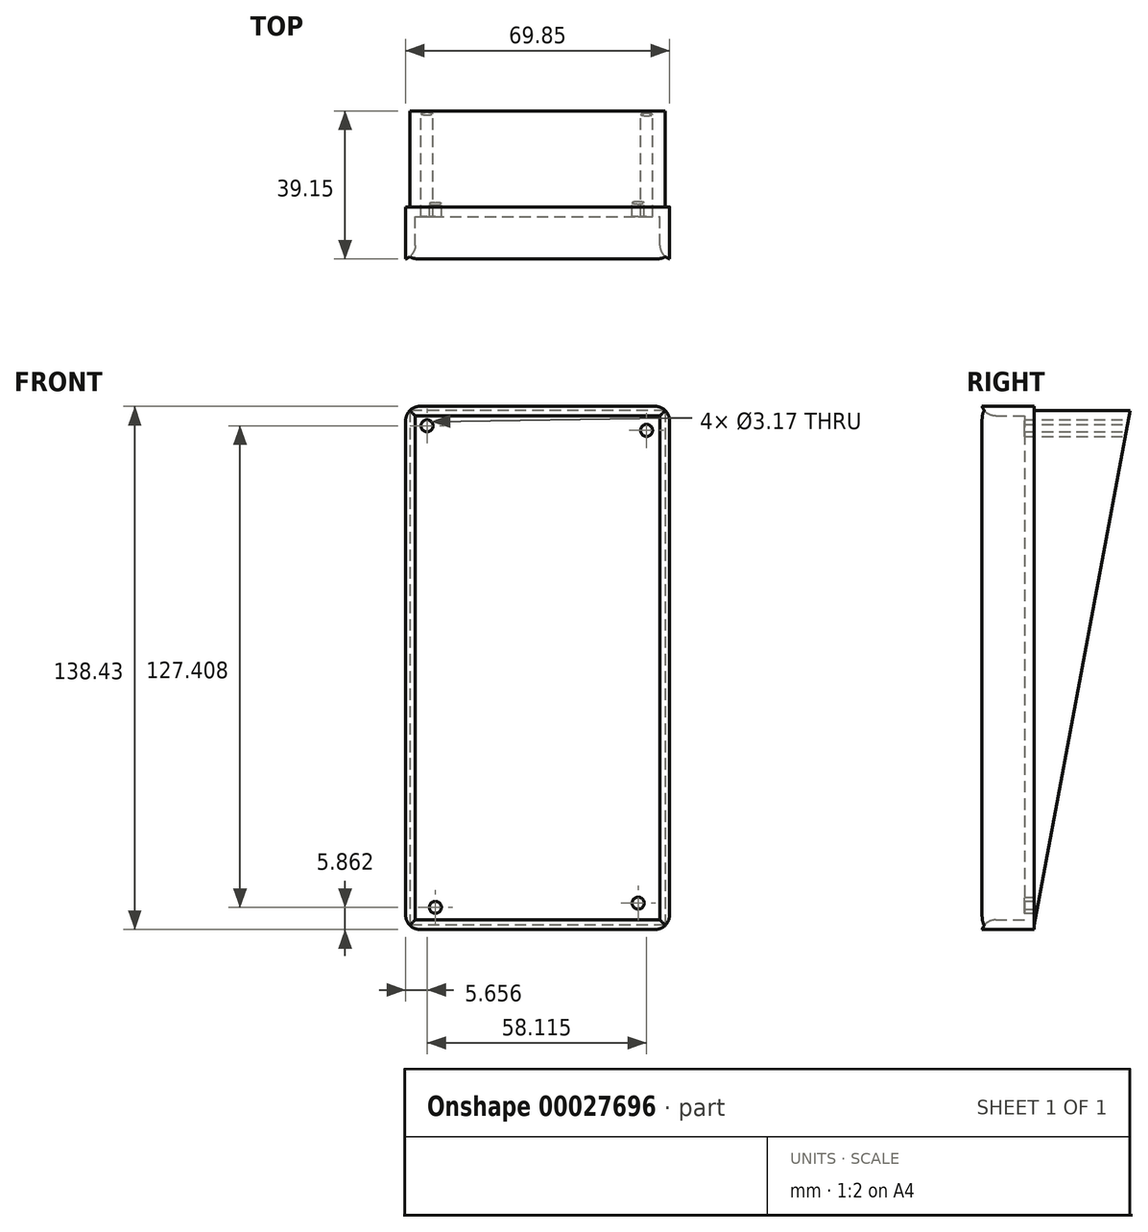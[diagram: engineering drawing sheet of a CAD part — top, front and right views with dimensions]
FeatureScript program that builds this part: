
annotation { "Feature Type Name" : "Feature", "Feature Type Description" : "" }
export const myFeature = defineFeature(function(context is Context, id is Id, definition is map)
    precondition{}
    {
        {
            var Q0;
            Q0=qCreatedBy(makeId("Front.planeOp"),FACE);
            var sketch = newSketch(context, id + "F0", { "sketchPlane" : qUnion([Q0])});
            skLineSegment(sketch, "E0.bottom", {"start": v(-34.53, 80.9) * mm, "end": v(35.32, 80.9) * mm});
            skLineSegment(sketch, "E0.top", {"start": v(-34.53, -57.52) * mm, "end": v(35.32, -57.52) * mm});
            skLineSegment(sketch, "E0.left", {"start": v(-34.53, 80.9) * mm, "end": v(-34.53, -57.52) * mm});
            skLineSegment(sketch, "E0.right", {"start": v(35.32, 80.9) * mm, "end": v(35.32, -57.52) * mm});
            skSolve(sketch);
        }
        {
            var Q0;
            Q0 = qSketchRegion(id + "F0", true);
            extrude(context, id + "F1", {"entities" : qUnion([Q0]), "depth" : 13.97 * mm});
        }
        {
            var Q0;
            Q0=makeQuery(id+"F1.opExtrude","CAP_FACE",FACE,{"disambiguationData":[OSD([sQuery(id+"F0.wireOp",EDGE,"E0.bottom"),sQuery(id+"F0.wireOp",EDGE,"E0.top"),sQuery(id+"F0.wireOp",EDGE,"E0.left"),sQuery(id+"F0.wireOp",EDGE,"E0.right")])],"isStart":false});
            shell(context, id + "F2", {"entities" : qUnion([Q0]), "thickness" : 2.54 * mm});
        }
        {
            var Q0;
            {var subQ0=sQuery(id+"F0.wireOp",EDGE,"E0.bottom");Q0=makeQuery(id+"F2.opShell","OFFSET_EDGE",EDGE,{"disambiguationData":[OSD([subQ0]),TDD([makeQuery(id+"F1.opExtrude","CAP_EDGE",EDGE,{"disambiguationData":[OSD([subQ0])],"isStart":false})])]});}
            var Q1;
            {var subQ0=sQuery(id+"F0.wireOp",EDGE,"E0.left");Q1=makeQuery(id+"F2.opShell","OFFSET_EDGE",EDGE,{"disambiguationData":[OSD([subQ0]),TDD([makeQuery(id+"F1.opExtrude","CAP_EDGE",EDGE,{"disambiguationData":[OSD([subQ0])],"isStart":false})])]});}
            var Q2;
            {var subQ0=sQuery(id+"F0.wireOp",EDGE,"E0.right");Q2=makeQuery(id+"F2.opShell","OFFSET_EDGE",EDGE,{"disambiguationData":[OSD([subQ0]),TDD([makeQuery(id+"F1.opExtrude","CAP_EDGE",EDGE,{"disambiguationData":[OSD([subQ0])],"isStart":false})])]});}
            var Q3;
            {var subQ0=sQuery(id+"F0.wireOp",EDGE,"E0.top");Q3=makeQuery(id+"F2.opShell","OFFSET_EDGE",EDGE,{"disambiguationData":[OSD([subQ0]),TDD([makeQuery(id+"F1.opExtrude","CAP_EDGE",EDGE,{"disambiguationData":[OSD([subQ0])],"isStart":false})])]});}
            var Q4;
            Q4=makeQuery(id+"F1.opExtrude","SWEPT_EDGE",EDGE,{"disambiguationData":[OSD([sQuery(id+"F0.wireOp",EDGE,"E0.top"),sQuery(id+"F0.wireOp",EDGE,"E0.left")])]});
            var Q5;
            Q5=makeQuery(id+"F1.opExtrude","SWEPT_EDGE",EDGE,{"disambiguationData":[OSD([sQuery(id+"F0.wireOp",EDGE,"E0.top"),sQuery(id+"F0.wireOp",EDGE,"E0.right")])]});
            var Q6;
            Q6=makeQuery(id+"F1.opExtrude","SWEPT_EDGE",EDGE,{"disambiguationData":[OSD([sQuery(id+"F0.wireOp",EDGE,"E0.bottom"),sQuery(id+"F0.wireOp",EDGE,"E0.left")])]});
            var Q7;
            Q7=makeQuery(id+"F1.opExtrude","SWEPT_EDGE",EDGE,{"disambiguationData":[OSD([sQuery(id+"F0.wireOp",EDGE,"E0.bottom"),sQuery(id+"F0.wireOp",EDGE,"E0.right")])]});
            fillet(context, id + "F3", {"entities" : qUnion([Q0, Q1, Q2, Q3, Q4, Q5, Q6, Q7]), "radius" : 3.8 * mm, "tangentPropagation" : true, "allowEdgeOverflow" : false});
        }
        {
            var Q0;
            Q0=makeQuery(id+"F1.opExtrude","CAP_FACE",FACE,{"disambiguationData":[OSD([sQuery(id+"F0.wireOp",EDGE,"E0.bottom"),sQuery(id+"F0.wireOp",EDGE,"E0.top"),sQuery(id+"F0.wireOp",EDGE,"E0.left"),sQuery(id+"F0.wireOp",EDGE,"E0.right")])],"isStart":true});
            var sketch = newSketch(context, id + "F4", { "sketchPlane" : qUnion([Q0])});
            skLineSegment(sketch, "E1.bottom", {"start": v(-34.2, 79.8) * mm, "end": v(33.42, 79.8) * mm});
            skLineSegment(sketch, "E1.top", {"start": v(-34.2, -56.4) * mm, "end": v(33.42, -56.4) * mm});
            skLineSegment(sketch, "E1.left", {"start": v(-34.2, 79.8) * mm, "end": v(-34.2, -56.4) * mm});
            skLineSegment(sketch, "E1.right", {"start": v(33.42, 79.8) * mm, "end": v(33.42, -56.4) * mm});
            skSolve(sketch);
        }
        {
            var Q0;
            Q0=makeQuery(id+"F4.imprint","IMPRINT",FACE,{"disambiguationData":[TD([[makeQuery(id+"F4.imprint","IMPRINT",EDGE,{"derivedFrom":sQuery(id+"F4.wireOp",EDGE,"E1.bottom")}),-1.0]])]});
            extrude(context, id + "F5", {"entities" : qUnion([Q0]), "operationType" : NewBodyOperationType.ADD, "depth" : 50.8 * mm});
        }
        {
            var Q0;
            Q0=makeQuery(id+"F5.opExtrude","SWEPT_FACE",FACE,{"disambiguationData":[OSD([sQuery(id+"F4.wireOp",EDGE,"E1.left")])]});
            var sketch = newSketch(context, id + "F6", { "sketchPlane" : qUnion([Q0])});
            skLineSegment(sketch, "E2", {"start": v(25.4, 79.8) * mm, "end": v(0, -56.4) * mm});
            skSolve(sketch);
        }
        {
            var Q0;
            Q0=makeQuery(id+"F5.opExtrude","CAP_FACE",FACE,{"disambiguationData":[OSD([sQuery(id+"F4.wireOp",EDGE,"E1.bottom"),sQuery(id+"F4.wireOp",EDGE,"E1.top"),sQuery(id+"F4.wireOp",EDGE,"E1.left"),sQuery(id+"F4.wireOp",EDGE,"E1.right")])],"isStart":false});
            var sketch = newSketch(context, id + "F7", { "sketchPlane" : qUnion([Q0])});
            skSolve(sketch);
        }
        {
            var Q0;
            Q0 = qSketchRegion(id + "F7", true);
            var Q1;
            {var subQ6=sQuery(id+"F6.wireOp",EDGE,"E2");Q1=makeQuery(id+"F6.imprint","IMPRINT",FACE,{"disambiguationData":[TD([[makeQuery(id+"F6.imprint","IMPRINT",EDGE,{"derivedFrom":subQ6}),1.0]])]});}
            extrude(context, id + "F8", {"entities" : qUnion([Q0, Q1]), "operationType" : NewBodyOperationType.ADD, "depth" : 25.4 * mm});
        }
        {
            var Q0;
            Q0=makeQuery(id+"F8.opExtrude","CAP_FACE",FACE,{"disambiguationData":[OSD([sQuery(id+"F0.wireOp",EDGE,"E0.bottom"),sQuery(id+"F0.wireOp",EDGE,"E0.top"),sQuery(id+"F0.wireOp",EDGE,"E0.left"),sQuery(id+"F0.wireOp",EDGE,"E0.right"),sQuery(id+"F4.wireOp",EDGE,"E1.bottom"),sQuery(id+"F4.wireOp",EDGE,"E1.top"),sQuery(id+"F4.wireOp",EDGE,"E1.left"),sQuery(id+"F6.wireOp",EDGE,"E2")])],"isStart":false});
            extrude(context, id + "F9", {"entities" : qUnion([Q0]), "operationType" : NewBodyOperationType.REMOVE, "oppositeDirection" : true, "depth" : 138.43 * mm});
        }
        {
            var Q0;
            Q0=makeQuery(id+"F7.imprint","IMPRINT",FACE,{"disambiguationData":[TD([[makeQuery(id+"F7.imprint","IMPRINT",EDGE,{"derivedFrom":makeQuery(id+"F5.opExtrude","CAP_EDGE",EDGE,{"disambiguationData":[OSD([sQuery(id+"F4.wireOp",EDGE,"E1.bottom")])],"isStart":false})}),-1.0]])]});
            var sketch = newSketch(context, id + "F10", { "sketchPlane" : qUnion([Q0])});
            skCircle(sketch, "E3", {"center": v(-29.08, 74.94) * mm, "radius": 1.59 * mm});
            skCircle(sketch, "E4", {"center": v(28.87, 75.75) * mm, "radius": 1.59 * mm});
            skCircle(sketch, "E5", {"center": v(28.87, -53.07) * mm, "radius": 1.59 * mm});
            skCircle(sketch, "E6", {"center": v(-30.9, -53.07) * mm, "radius": 1.59 * mm});
            skSolve(sketch);
        }
        {
            var Q0;
            Q0 = qSketchRegion(id + "FXB7eujVNJwT0vM_1", true);
            var Q1;
            Q1=makeQuery(id+"F10.imprint","IMPRINT",FACE,{"disambiguationData":[TD([[makeQuery(id+"F10.imprint","IMPRINT",EDGE,{"derivedFrom":sQuery(id+"F10.wireOp",EDGE,"E4")}),1.0]])]});
            extrude(context, id + "F11", {"entities" : qUnion([Q0, Q1]), "operationType" : NewBodyOperationType.REMOVE, "oppositeDirection" : true, "depth" : 101.6 * mm});
        }
        {
            var Q0;
            Q0=makeQuery(id+"F7.imprint","IMPRINT",FACE,{"disambiguationData":[TD([[makeQuery(id+"F7.imprint","IMPRINT",EDGE,{"derivedFrom":makeQuery(id+"F5.opExtrude","CAP_EDGE",EDGE,{"disambiguationData":[OSD([sQuery(id+"F4.wireOp",EDGE,"E1.bottom")])],"isStart":false})}),-1.0]])]});
            var sketch = newSketch(context, id + "F12", { "sketchPlane" : qUnion([Q0])});
            skCircle(sketch, "E7", {"center": v(-107.28, 233.25) * mm, "radius": 5.08 * mm});
            skCircle(sketch, "E8", {"center": v(-107.28, -210.96) * mm, "radius": 6.6 * mm});
            skCircle(sketch, "E9", {"center": v(107.39, -209.6) * mm, "radius": 5.68 * mm});
            skCircle(sketch, "E10", {"center": v(-29.24, 74.53) * mm, "radius": 1.59 * mm});
            skCircle(sketch, "E11", {"center": v(-27.02, -50.55) * mm, "radius": 1.59 * mm});
            skCircle(sketch, "E12", {"center": v(29.82, -52.3) * mm, "radius": 1.59 * mm});
            skSolve(sketch);
        }
        {
            var Q0;
            Q0=makeQuery(id+"F12.imprint","IMPRINT",FACE,{"disambiguationData":[TD([[makeQuery(id+"F12.imprint","IMPRINT",EDGE,{"derivedFrom":sQuery(id+"F12.wireOp",EDGE,"E11")}),1.0]])]});
            var Q1;
            Q1=makeQuery(id+"F12.imprint","IMPRINT",FACE,{"disambiguationData":[TD([[makeQuery(id+"F12.imprint","IMPRINT",EDGE,{"derivedFrom":sQuery(id+"F12.wireOp",EDGE,"E10")}),1.0]])]});
            extrude(context, id + "F13", {"entities" : qUnion([Q0, Q1]), "operationType" : NewBodyOperationType.REMOVE, "oppositeDirection" : true, "depth" : 101.6 * mm});
        }
        {
            var Q0;
            Q0=makeQuery(id+"F7.imprint","IMPRINT",FACE,{"disambiguationData":[TD([[makeQuery(id+"F7.imprint","IMPRINT",EDGE,{"derivedFrom":makeQuery(id+"F5.opExtrude","CAP_EDGE",EDGE,{"disambiguationData":[OSD([sQuery(id+"F4.wireOp",EDGE,"E1.bottom")])],"isStart":false})}),-1.0]])]});
            var sketch = newSketch(context, id + "F14", { "sketchPlane" : qUnion([Q0])});
            skCircle(sketch, "E13", {"center": v(26.65, -51.66) * mm, "radius": 1.59 * mm});
            skSolve(sketch);
        }
        {
            var Q0;
            Q0 = qSketchRegion(id + "F14", true);
            extrude(context, id + "F15", {"entities" : qUnion([Q0]), "operationType" : NewBodyOperationType.REMOVE, "oppositeDirection" : true, "depth" : 101.6 * mm});
        }
    });
